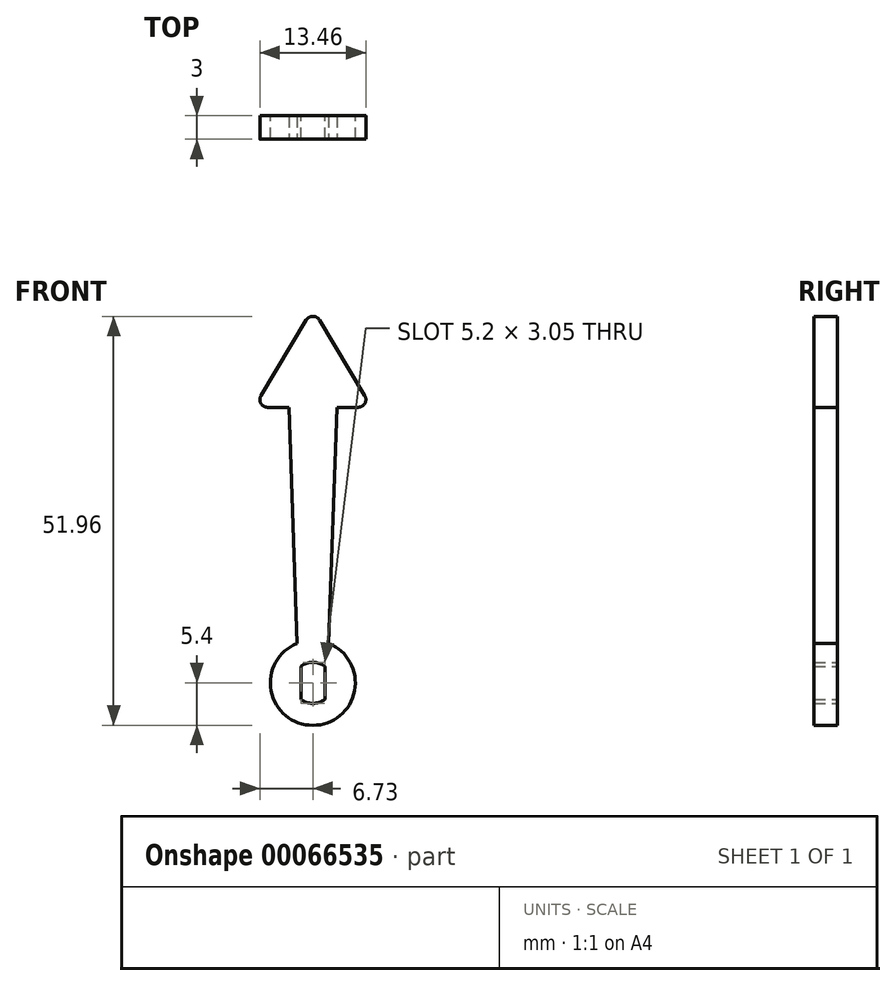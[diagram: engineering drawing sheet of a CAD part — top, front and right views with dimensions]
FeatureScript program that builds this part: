
annotation { "Feature Type Name" : "Feature", "Feature Type Description" : "" }
export const myFeature = defineFeature(function(context is Context, id is Id, definition is map)
    precondition{}
    {
        {
            var Q0;
            Q0=qCreatedBy(makeId("Front.planeOp"),FACE);
            var sketch = newSketch(context, id + "F0", { "sketchPlane" : qUnion([Q0])});
            skCircle(sketch, "E0", {"center": v(0, 0) * mm, "radius": 5.4 * mm});
            skCircle(sketch, "E1", {"center": v(0, 0) * mm, "radius": 2.6 * mm});
            skLineSegment(sketch, "E2", {"start": v(-1.53, 2.1) * mm, "end": v(-1.53, -2.1) * mm});
            skLineSegment(sketch, "E3", {"start": v(1.52, 2.1) * mm, "end": v(1.52, -2.1) * mm});
            skSolve(sketch);
        }
        {
            var Q0;
            {var subQ0=sQuery(id+"F0.wireOp",EDGE,"E2");Q0=makeQuery(id+"F0.imprint","IMPRINT",FACE,{"disambiguationData":[TD([[makeQuery(id+"F0.imprint","IMPRINT",EDGE,{"derivedFrom":subQ0}),-1.0]])]});}
            var Q1;
            Q1=makeQuery(id+"F0.imprint","IMPRINT",FACE,{"disambiguationData":[TD([[makeQuery(id+"F0.imprint","IMPRINT",EDGE,{"derivedFrom":sQuery(id+"F0.wireOp",EDGE,"E0")}),1.0]])]});
            var Q2;
            {var subQ0=sQuery(id+"F0.wireOp",EDGE,"E3");Q2=makeQuery(id+"F0.imprint","IMPRINT",FACE,{"disambiguationData":[TD([[makeQuery(id+"F0.imprint","IMPRINT",EDGE,{"derivedFrom":subQ0}),1.0]])]});}
            extrude(context, id + "F1", {"entities" : qUnion([Q0, Q1, Q2]), "endBound" : BoundingType.SYMMETRIC, "depth" : 3 * mm});
        }
        {
            var Q0;
            Q0=makeQuery(id+"F1.opExtrude","CAP_FACE",FACE,{"disambiguationData":[OSD([sQuery(id+"F0.wireOp",EDGE,"E1"),sQuery(id+"F0.wireOp",EDGE,"E2"),sQuery(id+"F0.wireOp",EDGE,"E3")])],"isStart":false});
            var sketch = newSketch(context, id + "F2", { "sketchPlane" : qUnion([Q0])});
            skLineSegment(sketch, "E4", {"start": v(0, 0) * mm, "end": v(0, 35) * mm, "construction": true});
            skLineSegment(sketch, "E5", {"start": v(0, 5.02) * mm, "end": v(2, 5.02) * mm});
            skLineSegment(sketch, "E6", {"start": v(2, 5.02) * mm, "end": v(3.05, 35) * mm});
            skLineSegment(sketch, "E7", {"start": v(0, 35) * mm, "end": v(3.05, 35) * mm});
            skLineSegment(sketch, "E8.MirrorCS", {"start": v(0, 35) * mm, "end": v(-3.05, 35) * mm});
            skLineSegment(sketch, "E9.MirrorCS", {"start": v(-2, 5.02) * mm, "end": v(-3.05, 35) * mm});
            skLineSegment(sketch, "E10.MirrorCS", {"start": v(0, 5.02) * mm, "end": v(-2, 5.02) * mm});
            skSolve(sketch);
        }
        {
            var Q0;
            {var subQ1=sQuery(id+"F2.wireOp",EDGE,"E6");Q0=makeQuery(id+"F2.imprint","IMPRINT",FACE,{"disambiguationData":[TD([[makeQuery(id+"F2.imprint","IMPRINT",EDGE,{"derivedFrom":subQ1}),1.0]])]});}
            var Q1;
            Q1=makeQuery(id+"F1.opExtrude","CAP_FACE",FACE,{"disambiguationData":[OSD([sQuery(id+"F0.wireOp",EDGE,"E0"),sQuery(id+"F0.wireOp",EDGE,"E1"),sQuery(id+"F0.wireOp",EDGE,"E2"),sQuery(id+"F0.wireOp",EDGE,"E3")])],"isStart":true});
            extrude(context, id + "F3", {"entities" : qUnion([Q0]), "operationType" : NewBodyOperationType.ADD, "endBound" : BoundingType.UP_TO_SURFACE, "oppositeDirection" : true, "endBoundEntityFace" : qUnion([Q1]), "depth" : 25 * mm});
        }
        {
            var Q0;
            {var subQ0=sQuery(id+"F0.wireOp",EDGE,"E0");Q0=makeQuery(id+"F3.boolean.opBoolean","MERGE",FACE,{"derivedFrom":[makeQuery(id+"F1.opExtrude","CAP_FACE",FACE,{"disambiguationData":[OSD([subQ0,sQuery(id+"F0.wireOp",EDGE,"E1"),sQuery(id+"F0.wireOp",EDGE,"E2"),sQuery(id+"F0.wireOp",EDGE,"E3")])],"isStart":false}),makeQuery(id+"F3.opExtrude","CAP_FACE",FACE,{"disambiguationData":[OSD([subQ0,sQuery(id+"F2.wireOp",EDGE,"E6"),sQuery(id+"F2.wireOp",EDGE,"E7"),sQuery(id+"F2.wireOp",EDGE,"E8.MirrorCS"),sQuery(id+"F2.wireOp",EDGE,"E9.MirrorCS")])],"isStart":true})]});}
            var sketch = newSketch(context, id + "F4", { "sketchPlane" : qUnion([Q0])});
            skLineSegment(sketch, "E11", {"start": v(0, 35) * mm, "end": v(0, 47.5) * mm, "construction": true});
            skLineSegment(sketch, "E12", {"start": v(-7.5, 35) * mm, "end": v(7.5, 35) * mm});
            skLineSegment(sketch, "E13", {"start": v(7.5, 35) * mm, "end": v(0, 47.5) * mm});
            skLineSegment(sketch, "E14", {"start": v(-7.5, 35) * mm, "end": v(0, 47.5) * mm});
            skSolve(sketch);
        }
        {
            var Q0;
            {var subQ0=sQuery(id+"F4.wireOp",EDGE,"E13");Q0=makeQuery(id+"F4.imprint","IMPRINT",FACE,{"disambiguationData":[TD([[makeQuery(id+"F4.imprint","IMPRINT",EDGE,{"derivedFrom":subQ0}),1.0]])]});}
            var Q1;
            {var subQ0=sQuery(id+"F0.wireOp",EDGE,"E0");Q1=makeQuery(id+"F3.boolean.opBoolean","MERGE",FACE,{"derivedFrom":[makeQuery(id+"F1.opExtrude","CAP_FACE",FACE,{"disambiguationData":[OSD([subQ0,sQuery(id+"F0.wireOp",EDGE,"E1"),sQuery(id+"F0.wireOp",EDGE,"E2"),sQuery(id+"F0.wireOp",EDGE,"E3")])],"isStart":true}),makeQuery(id+"F3.opExtrude","CAP_FACE",FACE,{"disambiguationData":[OSD([subQ0,sQuery(id+"F2.wireOp",EDGE,"E6"),sQuery(id+"F2.wireOp",EDGE,"E7"),sQuery(id+"F2.wireOp",EDGE,"E8.MirrorCS"),sQuery(id+"F2.wireOp",EDGE,"E9.MirrorCS")])],"isStart":false})]});}
            extrude(context, id + "F5", {"entities" : qUnion([Q0]), "operationType" : NewBodyOperationType.ADD, "endBound" : BoundingType.UP_TO_SURFACE, "oppositeDirection" : true, "endBoundEntityFace" : qUnion([Q1]), "depth" : 25 * mm});
        }
        {
            var Q0;
            Q0=makeQuery(id+"F5.opExtrude","SWEPT_EDGE",EDGE,{"disambiguationData":[OSD([sQuery(id+"F4.wireOp",EDGE,"E12"),sQuery(id+"F4.wireOp",EDGE,"E13")])]});
            var Q1;
            Q1=makeQuery(id+"F5.opExtrude","SWEPT_EDGE",EDGE,{"disambiguationData":[OSD([sQuery(id+"F4.wireOp",EDGE,"E12"),sQuery(id+"F4.wireOp",EDGE,"E14")])]});
            var Q2;
            Q2=makeQuery(id+"F5.opExtrude","SWEPT_EDGE",EDGE,{"disambiguationData":[OSD([sQuery(id+"F4.wireOp",EDGE,"E13"),sQuery(id+"F4.wireOp",EDGE,"E14")])]});
            fillet(context, id + "F6", {"entities" : qUnion([Q0, Q1, Q2]), "radius" : 1 * mm, "tangentPropagation" : true, "allowEdgeOverflow" : false});
        }
    });
